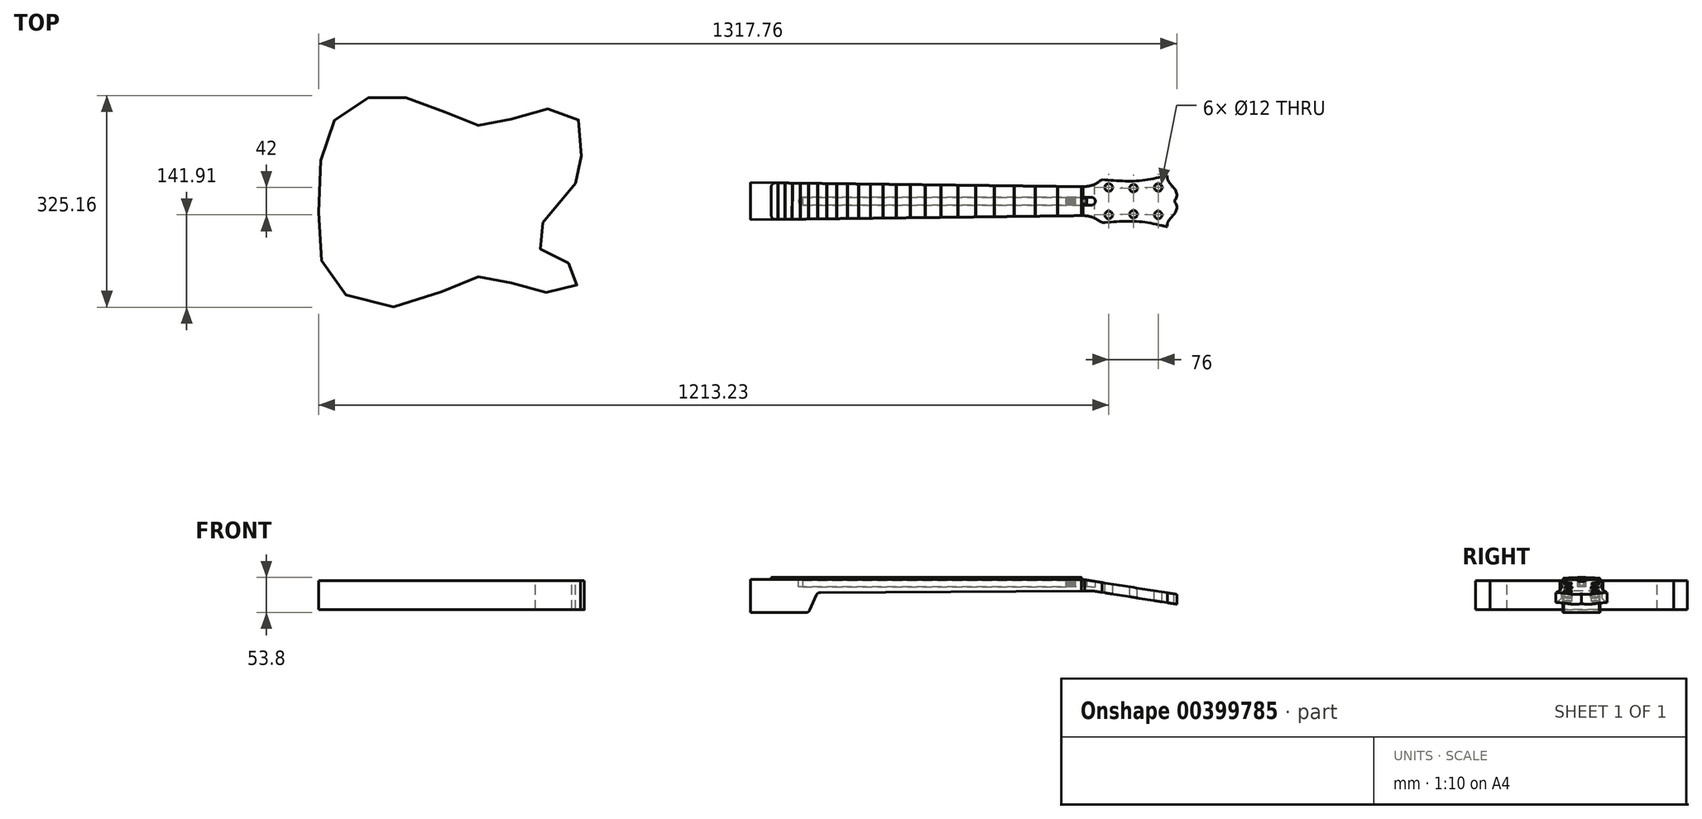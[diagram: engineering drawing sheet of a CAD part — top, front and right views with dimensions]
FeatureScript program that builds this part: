
annotation { "Feature Type Name" : "Feature", "Feature Type Description" : "" }
export const myFeature = defineFeature(function(context is Context, id is Id, definition is map)
    precondition{}
    {
        {
            var Q0;
            Q0=qCreatedBy(makeId("Top.planeOp"),FACE);
            var sketch = newSketch(context, id + "F0", { "sketchPlane" : qUnion([Q0])});
            skLineSegment(sketch, "E0", {"start": v(-323.85, 0) * mm, "end": v(323.85, 0) * mm, "construction": true});
            skLineSegment(sketch, "E1", {"start": v(323.85, 22.23) * mm, "end": v(323.85, -22.22) * mm, "construction": true});
            skLineSegment(sketch, "E2", {"start": v(-323.85, 26.25) * mm, "end": v(-323.85, -26.25) * mm, "construction": true});
            skLineSegment(sketch, "E3", {"start": v(-323.85, 26.25) * mm, "end": v(-323.85, 30.25) * mm, "construction": true});
            skLineSegment(sketch, "E4.MirrorCS", {"start": v(-323.85, -26.25) * mm, "end": v(-323.85, -30.25) * mm, "construction": true});
            skLineSegment(sketch, "E5", {"start": v(-323.85, 30.25) * mm, "end": v(323.85, 22.23) * mm, "construction": true});
            skLineSegment(sketch, "E6", {"start": v(-323.85, -30.25) * mm, "end": v(323.85, -22.23) * mm, "construction": true});
            skPoint(sketch, "E7", {"position": v(287.5, 0) * mm});
            skPoint(sketch, "E8", {"position": v(253.19, 0) * mm});
            skPoint(sketch, "E9", {"position": v(220.8, 0) * mm});
            skPoint(sketch, "E10", {"position": v(190.22, 0) * mm});
            skPoint(sketch, "E11", {"position": v(161.37, 0) * mm});
            skPoint(sketch, "E12", {"position": v(134.14, 0) * mm});
            skPoint(sketch, "E13", {"position": v(108.43, 0) * mm});
            skPoint(sketch, "E14", {"position": v(84.18, 0) * mm});
            skPoint(sketch, "E15", {"position": v(61.26, 0) * mm});
            skPoint(sketch, "E16", {"position": v(39.65, 0) * mm});
            skPoint(sketch, "E17", {"position": v(19.25, 0) * mm});
            skPoint(sketch, "E18", {"position": v(0, 0) * mm});
            skPoint(sketch, "E19", {"position": v(-18.19, 0) * mm});
            skPoint(sketch, "E20", {"position": v(-35.33, 0) * mm});
            skPoint(sketch, "E21", {"position": v(-51.54, 0) * mm});
            skPoint(sketch, "E22", {"position": v(-66.83, 0) * mm});
            skPoint(sketch, "E23", {"position": v(-81.25, 0) * mm});
            skPoint(sketch, "E24", {"position": v(-94.87, 0) * mm});
            skPoint(sketch, "E25", {"position": v(-107.72, 0) * mm});
            skPoint(sketch, "E26", {"position": v(-119.86, 0) * mm});
            skPoint(sketch, "E27", {"position": v(-131.32, 0) * mm});
            skPoint(sketch, "E28", {"position": v(-142.11, 0) * mm});
            skPoint(sketch, "E29", {"position": v(-152.32, 0) * mm});
            skLineSegment(sketch, "E30", {"start": v(-152.32, 0) * mm, "end": v(-152.32, -28.13) * mm, "construction": true});
            skLineSegment(sketch, "E31", {"start": v(-152.32, -28.13) * mm, "end": v(-152.32, 28.13) * mm, "construction": true});
            skLineSegment(sketch, "E32", {"start": v(-142.11, 0) * mm, "end": v(-142.11, -28) * mm, "construction": true});
            skLineSegment(sketch, "E33", {"start": v(-142.11, -28) * mm, "end": v(-142.11, 28) * mm, "construction": true});
            skLineSegment(sketch, "E34", {"start": v(-142.11, 28) * mm, "end": v(-131.32, 27.87) * mm, "construction": true});
            skLineSegment(sketch, "E35", {"start": v(-131.32, 0) * mm, "end": v(-131.32, -27.87) * mm, "construction": true});
            skLineSegment(sketch, "E36", {"start": v(-131.32, -27.87) * mm, "end": v(-131.32, 27.87) * mm, "construction": true});
            skLineSegment(sketch, "E37", {"start": v(-119.86, 0) * mm, "end": v(-120.2, -27.73) * mm, "construction": true});
            skLineSegment(sketch, "E38", {"start": v(-107.72, 0) * mm, "end": v(-107.72, 27.57) * mm, "construction": true});
            skLineSegment(sketch, "E39", {"start": v(-107.72, 27.57) * mm, "end": v(-107.72, -27.57) * mm, "construction": true});
            skLineSegment(sketch, "E40", {"start": v(-94.87, 0) * mm, "end": v(-94.87, 27.41) * mm, "construction": true});
            skLineSegment(sketch, "E41", {"start": v(-94.87, 27.41) * mm, "end": v(-94.87, -27.41) * mm, "construction": true});
            skLineSegment(sketch, "E42", {"start": v(-81.25, 0) * mm, "end": v(-81.25, 27.24) * mm, "construction": true});
            skLineSegment(sketch, "E43", {"start": v(-81.25, 27.24) * mm, "end": v(-81.25, -27.24) * mm, "construction": true});
            skLineSegment(sketch, "E44", {"start": v(-66.83, 0) * mm, "end": v(-66.83, 27.07) * mm, "construction": true});
            skLineSegment(sketch, "E45", {"start": v(-66.83, 27.07) * mm, "end": v(-66.83, -27.07) * mm, "construction": true});
            skLineSegment(sketch, "E46", {"start": v(-51.54, 0) * mm, "end": v(-51.54, 26.88) * mm, "construction": true});
            skLineSegment(sketch, "E47", {"start": v(-51.54, 26.88) * mm, "end": v(-51.54, -26.88) * mm, "construction": true});
            skLineSegment(sketch, "E48", {"start": v(-35.33, 0) * mm, "end": v(-35.33, 26.68) * mm, "construction": true});
            skLineSegment(sketch, "E49", {"start": v(-35.33, 26.68) * mm, "end": v(-35.33, -26.68) * mm, "construction": true});
            skLineSegment(sketch, "E50", {"start": v(-18.19, 0) * mm, "end": v(-18.19, 26.46) * mm, "construction": true});
            skLineSegment(sketch, "E51", {"start": v(-18.19, 26.46) * mm, "end": v(-18.19, -26.46) * mm, "construction": true});
            skLineSegment(sketch, "E52", {"start": v(19.25, 0) * mm, "end": v(19.25, 26) * mm, "construction": true});
            skLineSegment(sketch, "E53", {"start": v(19.25, 26) * mm, "end": v(19.25, -26) * mm, "construction": true});
            skLineSegment(sketch, "E54", {"start": v(39.65, 0) * mm, "end": v(39.65, 25.75) * mm, "construction": true});
            skLineSegment(sketch, "E55", {"start": v(39.65, 25.75) * mm, "end": v(39.65, -25.75) * mm, "construction": true});
            skLineSegment(sketch, "E56", {"start": v(61.26, 0) * mm, "end": v(61.26, 25.48) * mm, "construction": true});
            skLineSegment(sketch, "E57", {"start": v(61.26, 25.48) * mm, "end": v(61.26, -25.48) * mm, "construction": true});
            skLineSegment(sketch, "E58", {"start": v(84.18, 0) * mm, "end": v(84.18, 25.2) * mm, "construction": true});
            skLineSegment(sketch, "E59", {"start": v(84.18, 25.2) * mm, "end": v(84.18, -25.2) * mm, "construction": true});
            skLineSegment(sketch, "E60", {"start": v(108.43, 0) * mm, "end": v(108.43, 24.9) * mm, "construction": true});
            skLineSegment(sketch, "E61", {"start": v(108.43, 24.9) * mm, "end": v(108.43, -24.9) * mm, "construction": true});
            skLineSegment(sketch, "E62", {"start": v(134.14, 0) * mm, "end": v(134.14, 24.58) * mm, "construction": true});
            skLineSegment(sketch, "E63", {"start": v(134.14, 24.58) * mm, "end": v(134.14, -24.58) * mm, "construction": true});
            skLineSegment(sketch, "E64", {"start": v(161.37, 0) * mm, "end": v(161.37, 24.24) * mm, "construction": true});
            skLineSegment(sketch, "E65", {"start": v(161.37, 24.24) * mm, "end": v(161.37, -24.24) * mm, "construction": true});
            skLineSegment(sketch, "E66", {"start": v(190.22, 0) * mm, "end": v(190.22, 23.88) * mm, "construction": true});
            skLineSegment(sketch, "E67", {"start": v(190.22, 23.88) * mm, "end": v(190.22, -23.88) * mm, "construction": true});
            skLineSegment(sketch, "E68", {"start": v(220.8, 0) * mm, "end": v(220.8, 23.5) * mm});
            skLineSegment(sketch, "E69", {"start": v(220.8, 23.5) * mm, "end": v(220.8, -23.5) * mm, "construction": true});
            skLineSegment(sketch, "E70", {"start": v(253.19, 0) * mm, "end": v(253.19, 23.1) * mm, "construction": true});
            skLineSegment(sketch, "E71", {"start": v(253.19, 23.1) * mm, "end": v(253.19, -23.1) * mm, "construction": true});
            skLineSegment(sketch, "E72", {"start": v(287.5, 0) * mm, "end": v(287.5, 22.68) * mm, "construction": true});
            skLineSegment(sketch, "E73", {"start": v(287.5, 22.68) * mm, "end": v(287.5, -22.68) * mm, "construction": true});
            skLineSegment(sketch, "E74", {"start": v(0, 0) * mm, "end": v(0, 26.24) * mm, "construction": true});
            skLineSegment(sketch, "E75", {"start": v(0, 26.24) * mm, "end": v(0, -26.24) * mm, "construction": true});
            skLineSegment(sketch, "E76", {"start": v(-119.86, 0) * mm, "end": v(-119.86, 27.72) * mm, "construction": true});
            skLineSegment(sketch, "E77", {"start": v(323.85, 0) * mm, "end": v(-317.5, 0) * mm, "construction": true});
            skLineSegment(sketch, "E78", {"start": v(-317.08, 33.5) * mm, "end": v(-317.92, -33.5) * mm, "construction": true});
            skPoint(sketch, "E79", {"position": v(-317.08, 33.5) * mm});
            skPoint(sketch, "E80", {"position": v(-317.92, -33.5) * mm});
            skLineSegment(sketch, "E81", {"start": v(-317.08, 33.5) * mm, "end": v(-347.56, 33.88) * mm, "construction": true});
            skPoint(sketch, "E82", {"position": v(-347.56, 33.88) * mm});
            skLineSegment(sketch, "E83.MirrorCS", {"start": v(-317.08, -33.5) * mm, "end": v(-347.56, -33.88) * mm, "construction": true});
            skPoint(sketch, "E84.MirrorP", {"position": v(-347.56, -33.88) * mm});
            skLineSegment(sketch, "E85", {"start": v(-347.56, -33.88) * mm, "end": v(-347.56, 33.88) * mm, "construction": true});
            skPoint(sketch, "E86", {"position": v(-347.56, 0) * mm});
            skLineSegment(sketch, "E87", {"start": v(323.85, 0) * mm, "end": v(328.61, 0) * mm, "construction": true});
            skLineSegment(sketch, "E88", {"start": v(328.61, -22.22) * mm, "end": v(328.61, 22.23) * mm, "construction": true});
            skSolve(sketch);
        }
        {
            var Q0;
            Q0=qCreatedBy(makeId("Top.planeOp"),FACE);
            var sketch = newSketch(context, id + "F1", { "sketchPlane" : qUnion([Q0])});
            skLineSegment(sketch, "E89", {"start": v(-184.07, 44.45) * mm, "end": v(-184.07, -44.45) * mm, "construction": true});
            skPoint(sketch, "E90.0", {"position": v(-152.32, 0) * mm});
            skLineSegment(sketch, "E91", {"start": v(-152.32, 0) * mm, "end": v(-184.07, 0) * mm, "construction": true});
            skLineSegment(sketch, "E92.bottom", {"start": v(-184.07, 44.45) * mm, "end": v(476.33, 44.45) * mm});
            skLineSegment(sketch, "E92.top", {"start": v(-184.07, -44.45) * mm, "end": v(476.33, -44.45) * mm});
            skLineSegment(sketch, "E92.left", {"start": v(-184.07, 44.45) * mm, "end": v(-184.07, -44.45) * mm});
            skLineSegment(sketch, "E92.right", {"start": v(476.33, 44.45) * mm, "end": v(476.33, -44.45) * mm});
            skSolve(sketch);
        }
        {
            var Q0;
            Q0 = qSketchRegion(id + "F1", true);
            extrude(context, id + "F2", {"entities" : qUnion([Q0]), "oppositeDirection" : true, "depth" : 63.5 * mm});
        }
        {
            var Q0;
            Q0=makeQuery(id+"F2.opExtrude","CAP_FACE",FACE,{"disambiguationData":[OSD([sQuery(id+"F1.wireOp",EDGE,"E92.bottom"),sQuery(id+"F1.wireOp",EDGE,"E92.top"),sQuery(id+"F1.wireOp",EDGE,"E92.left"),sQuery(id+"F1.wireOp",EDGE,"E92.right")])],"isStart":true});
            cPlane(context, id + "F3", {"entities" : qUnion([Q0]), "cplaneType" : CPlaneType.OFFSET, "offset" : 2 * mm, "oppositeDirection" : true, "width" : 152.4 * mm, "height" : 152.4 * mm});
        }
        {
            var Q0;
            Q0=makeQuery(id+"F2.opExtrude","CAP_FACE",FACE,{"disambiguationData":[OSD([sQuery(id+"F1.wireOp",EDGE,"E92.bottom"),sQuery(id+"F1.wireOp",EDGE,"E92.top"),sQuery(id+"F1.wireOp",EDGE,"E92.left"),sQuery(id+"F1.wireOp",EDGE,"E92.right")])],"isStart":true});
            var sketch = newSketch(context, id + "F4", { "sketchPlane" : qUnion([Q0])});
            skPoint(sketch, "E93.0", {"position": v(326.23, 0) * mm});
            skLineSegment(sketch, "E94", {"start": v(326.23, 0) * mm, "end": v(345.28, 0) * mm, "construction": true});
            skLineSegment(sketch, "E95", {"start": v(326.23, 0) * mm, "end": v(-110.33, 0) * mm, "construction": true});
            skLineSegment(sketch, "E96", {"start": v(345.28, 0) * mm, "end": v(345.28, -6) * mm, "construction": true});
            skLineSegment(sketch, "E97.bottom", {"start": v(339.28, 6) * mm, "end": v(-104.33, 6) * mm});
            skLineSegment(sketch, "E97.top", {"start": v(339.28, -6) * mm, "end": v(-104.33, -6) * mm});
            skLineSegment(sketch, "E97.left", {"start": v(345.28, 6) * mm, "end": v(345.28, 0) * mm});
            skLineSegment(sketch, "E97.right", {"start": v(-110.33, 0) * mm, "end": v(-110.33, 0) * mm});
            skPoint(sketch, "E98.visualSharp", {"position": v(-110.33, 6) * mm});
            skArc(sketch, "E98.filletArc", {"start": v(-104.33, 6) * mm, "mid": v(-108.57, 4.24) * mm, "end": v(-110.33, 0) * mm});
            skPoint(sketch, "E99.visualSharp", {"position": v(-110.33, -6) * mm});
            skArc(sketch, "E99.filletArc", {"start": v(-110.33, 0) * mm, "mid": v(-108.57, -4.24) * mm, "end": v(-104.33, -6) * mm});
            skPoint(sketch, "E100.visualSharp", {"position": v(345.28, -6) * mm});
            skArc(sketch, "E100.filletArc", {"start": v(339.28, -6) * mm, "mid": v(343.52, -4.24) * mm, "end": v(345.28, 0) * mm});
            skPoint(sketch, "E101.visualSharp", {"position": v(345.28, 6) * mm});
            skArc(sketch, "E101.filletArc", {"start": v(345.28, 0) * mm, "mid": v(343.52, 4.24) * mm, "end": v(339.28, 6) * mm});
            skSolve(sketch);
        }
        {
            var Q0;
            Q0 = qSketchRegion(id + "F4", true);
            extrude(context, id + "F5", {"entities" : qUnion([Q0]), "operationType" : NewBodyOperationType.REMOVE, "oppositeDirection" : true, "depth" : 11.5 * mm});
        }
        {
            var Q0;
            Q0=makeQuery(id+"F2.opExtrude","SWEPT_FACE",FACE,{"disambiguationData":[OSD([sQuery(id+"F1.wireOp",EDGE,"E92.top")])]});
            var sketch = newSketch(context, id + "F6", { "sketchPlane" : qUnion([Q0])});
            skPoint(sketch, "E102.0", {"position": v(328.61, 0) * mm});
            skPoint(sketch, "E103.0", {"position": v(326.23, 0) * mm});
            skLineSegment(sketch, "E104", {"start": v(326.23, 0) * mm, "end": v(326.23, -63.5) * mm, "construction": true});
            skLineSegment(sketch, "E105", {"start": v(328.61, 0) * mm, "end": v(328.61, -63.5) * mm, "construction": true});
            skLineSegment(sketch, "E106", {"start": v(326.23, 0) * mm, "end": v(476.33, -23.77) * mm});
            skLineSegment(sketch, "E107", {"start": v(326.23, 0) * mm, "end": v(476.33, 0) * mm});
            skLineSegment(sketch, "E108", {"start": v(476.33, 0) * mm, "end": v(476.33, -23.77) * mm});
            skSolve(sketch);
        }
        {
            var Q0;
            Q0=makeQuery(id+"F6.imprint","IMPRINT",FACE,{"disambiguationData":[TD([[makeQuery(id+"F6.imprint","IMPRINT",EDGE,{"derivedFrom":sQuery(id+"F6.wireOp",EDGE,"E106")}),1.0]])]});
            var Q1;
            Q1=makeQuery(id+"F2.opExtrude","SWEPT_BODY",BODY,{"disambiguationData":[OSD([sQuery(id+"F1.wireOp",EDGE,"E92.bottom"),sQuery(id+"F1.wireOp",EDGE,"E92.top"),sQuery(id+"F1.wireOp",EDGE,"E92.left"),sQuery(id+"F1.wireOp",EDGE,"E92.right")])]});
            extrude(context, id + "F7", {"entities" : qUnion([Q0]), "operationType" : NewBodyOperationType.REMOVE, "endBound" : BoundingType.UP_TO_BODY, "oppositeDirection" : true, "endBoundEntityBody" : qUnion([Q1]), "depth" : 25.4 * mm});
        }
        {
            var Q0;
            Q0=makeQuery(id+"F2.opExtrude","SWEPT_FACE",FACE,{"disambiguationData":[OSD([sQuery(id+"F1.wireOp",EDGE,"E92.top")])]});
            var sketch = newSketch(context, id + "F8", { "sketchPlane" : qUnion([Q0])});
            skLineSegment(sketch, "E109", {"start": v(401.28, -11.89) * mm, "end": v(398.93, -26.7) * mm, "construction": true});
            skPoint(sketch, "E110.0", {"position": v(328.61, 0) * mm});
            skLineSegment(sketch, "E111.0", {"start": v(326.23, 0) * mm, "end": v(476.33, -23.77) * mm, "construction": true});
            skLineSegment(sketch, "E112", {"start": v(476.33, -23.77) * mm, "end": v(326.23, 0) * mm});
            skPoint(sketch, "E113.0", {"position": v(-119.86, 0) * mm});
            skLineSegment(sketch, "E114", {"start": v(-119.86, 0) * mm, "end": v(-119.86, -63.5) * mm, "construction": true});
            skLineSegment(sketch, "E115", {"start": v(326.23, 0) * mm, "end": v(326.23, -18) * mm, "construction": true});
            skPoint(sketch, "E116.0", {"position": v(-81.25, 0) * mm});
            skPoint(sketch, "E117.0", {"position": v(-94.87, 0) * mm});
            skLineSegment(sketch, "E118", {"start": v(-94.87, 0) * mm, "end": v(-94.87, -63.5) * mm, "construction": true});
            skLineSegment(sketch, "E119", {"start": v(-81.25, 0) * mm, "end": v(-81.25, -20) * mm, "construction": true});
            skLineSegment(sketch, "E120", {"start": v(-77.14, -19.98) * mm, "end": v(343.46, -17.92) * mm});
            skLineSegment(sketch, "E121", {"start": v(-82.92, -23.76) * mm, "end": v(-93.2, -47.02) * mm});
            skLineSegment(sketch, "E122", {"start": v(-99, -50.8) * mm, "end": v(-184.07, -50.8) * mm});
            skLineSegment(sketch, "E123", {"start": v(-184.07, -50.8) * mm, "end": v(-184.07, 0) * mm});
            skLineSegment(sketch, "E124", {"start": v(-184.07, 0) * mm, "end": v(328.61, 0) * mm});
            skPoint(sketch, "E125.visualSharp", {"position": v(-81.25, -20) * mm});
            skArc(sketch, "E125.filletArc", {"start": v(-77.14, -19.98) * mm, "mid": v(-80.59, -21.02) * mm, "end": v(-82.92, -23.76) * mm});
            skPoint(sketch, "E126.visualSharp", {"position": v(-94.87, -50.8) * mm});
            skArc(sketch, "E126.filletArc", {"start": v(-99, -50.8) * mm, "mid": v(-95.54, -49.77) * mm, "end": v(-93.2, -47.02) * mm});
            skLineSegment(sketch, "E127", {"start": v(473.98, -38.59) * mm, "end": v(343.46, -17.92) * mm});
            skLineSegment(sketch, "E128", {"start": v(476.33, -23.77) * mm, "end": v(470.03, -63.5) * mm});
            skSolve(sketch);
        }
        {
            var Q0;
            Q0 = qSketchRegion(id + "F8", true);
            var Q1;
            Q1=makeQuery(id+"F2.opExtrude","SWEPT_BODY",BODY,{"disambiguationData":[OSD([sQuery(id+"F1.wireOp",EDGE,"E92.bottom"),sQuery(id+"F1.wireOp",EDGE,"E92.top"),sQuery(id+"F1.wireOp",EDGE,"E92.left"),sQuery(id+"F1.wireOp",EDGE,"E92.right")])]});
            extrude(context, id + "F9", {"entities" : qUnion([Q0]), "operationType" : NewBodyOperationType.INTERSECT, "endBound" : BoundingType.UP_TO_BODY, "oppositeDirection" : true, "endBoundEntityBody" : qUnion([Q1]), "depth" : 101.6 * mm});
        }
        {
            var Q0;
            Q0=makeQuery(id+"F2.opExtrude","CAP_FACE",FACE,{"disambiguationData":[OSD([sQuery(id+"F1.wireOp",EDGE,"E92.bottom"),sQuery(id+"F1.wireOp",EDGE,"E92.top"),sQuery(id+"F1.wireOp",EDGE,"E92.left"),sQuery(id+"F1.wireOp",EDGE,"E92.right")])],"isStart":true});
            var sketch = newSketch(context, id + "F10", { "sketchPlane" : qUnion([Q0])});
            skLineSegment(sketch, "E129.0", {"start": v(323.85, 0) * mm, "end": v(-317.5, 0) * mm, "construction": true});
            skLineSegment(sketch, "E130", {"start": v(323.85, 0) * mm, "end": v(472.48, 0) * mm, "construction": true});
            skLineSegment(sketch, "E131.0", {"start": v(328.61, -22.22) * mm, "end": v(328.61, 22.23) * mm, "construction": true});
            skLineSegment(sketch, "E132.0", {"start": v(323.85, 22.23) * mm, "end": v(323.85, -22.22) * mm, "construction": true});
            skLineSegment(sketch, "E133", {"start": v(365.85, 0) * mm, "end": v(365.85, 21) * mm, "construction": true});
            skLineSegment(sketch, "E134", {"start": v(403.85, 0) * mm, "end": v(403.85, 20) * mm, "construction": true});
            skLineSegment(sketch, "E135", {"start": v(441.85, 0) * mm, "end": v(441.85, 21) * mm, "construction": true});
            skCircle(sketch, "E136", {"center": v(365.85, 21) * mm, "radius": 6 * mm});
            skCircle(sketch, "E137", {"center": v(403.85, 20) * mm, "radius": 6 * mm});
            skCircle(sketch, "E138", {"center": v(441.85, 21) * mm, "radius": 6 * mm});
            skCircle(sketch, "E139.MirrorC", {"center": v(365.85, -21) * mm, "radius": 6 * mm});
            skCircle(sketch, "E140.MirrorC", {"center": v(403.85, -20) * mm, "radius": 6 * mm});
            skCircle(sketch, "E141.MirrorC", {"center": v(441.85, -21) * mm, "radius": 6 * mm});
            skLineSegment(sketch, "E142", {"start": v(365.85, -21) * mm, "end": v(355.85, -21) * mm, "construction": true});
            skLineSegment(sketch, "E143", {"start": v(355.85, -21) * mm, "end": v(355.85, -33) * mm, "construction": true});
            skLineSegment(sketch, "E144", {"start": v(355.85, -33) * mm, "end": v(470.76, -33) * mm, "construction": true});
            skPoint(sketch, "E145", {"position": v(465.77, 0) * mm});
            skPoint(sketch, "E146", {"position": v(455.61, -39.35) * mm});
            skFitSpline(sketch, "E147", {"points": [v(465.77, 0) * mm, v(469.92, -13.07) * mm, v(458.58, -28.8) * mm, v(455.61, -39.35) * mm], "startDerivative": vector(34.11, -22.35) * mm, "endDerivative": vector(7.21, -32.63) * mm});
            skFitSpline(sketch, "E148", {"points": [v(455.61, -39.35) * mm, v(411.53, -31.35) * mm, v(355.85, -33) * mm], "startDerivative": vector(-90.96, 21.97) * mm, "endDerivative": vector(-108.28, -8.76) * mm});
            skFitSpline(sketch, "E149", {"points": [v(328.61, -22.22) * mm, v(342.64, -25.24) * mm, v(355.85, -33) * mm], "startDerivative": vector(28.5, -4.66) * mm, "endDerivative": vector(25.97, -12.88) * mm});
            skFitSpline(sketch, "E150.MirrorCS", {"points": [v(328.61, 22.22) * mm, v(342.64, 25.24) * mm, v(355.85, 33) * mm], "startDerivative": vector(28.5, 4.66) * mm, "endDerivative": vector(25.97, 12.88) * mm});
            skFitSpline(sketch, "E151.MirrorCS", {"points": [v(455.61, 39.35) * mm, v(411.53, 31.35) * mm, v(355.85, 33) * mm], "startDerivative": vector(-90.96, -21.97) * mm, "endDerivative": vector(-108.28, 8.76) * mm});
            skFitSpline(sketch, "E152.MirrorCS", {"points": [v(465.77, 0) * mm, v(469.92, 13.07) * mm, v(458.58, 28.8) * mm, v(455.61, 39.35) * mm], "startDerivative": vector(34.11, 22.35) * mm, "endDerivative": vector(7.21, 32.63) * mm});
            skLineSegment(sketch, "E153", {"start": v(328.61, 22.23) * mm, "end": v(323.85, 22.23) * mm});
            skPoint(sketch, "E154.0", {"position": v(-152.32, 28.13) * mm});
            skPoint(sketch, "E155.0", {"position": v(-152.32, -28.13) * mm});
            skLineSegment(sketch, "E156", {"start": v(323.85, 22.23) * mm, "end": v(-184.07, 28.52) * mm});
            skLineSegment(sketch, "E157", {"start": v(-184.07, -28.52) * mm, "end": v(323.85, -22.22) * mm});
            skLineSegment(sketch, "E158", {"start": v(323.85, -22.22) * mm, "end": v(328.61, -22.22) * mm});
            skLineSegment(sketch, "E159", {"start": v(-184.07, 28.52) * mm, "end": v(-184.07, -28.52) * mm});
            skSolve(sketch);
        }
        {
            var Q0;
            Q0=makeQuery(id+"F10.imprint","IMPRINT",FACE,{"disambiguationData":[TD([[makeQuery(id+"F10.imprint","IMPRINT",EDGE,{"derivedFrom":sQuery(id+"F10.wireOp",EDGE,"E136")}),-1.0]])]});
            var Q1;
            {var subQ12=sQuery(id+"F10.wireOp",EDGE,"E156");Q1=makeQuery(id+"F10.imprint","IMPRINT",FACE,{"disambiguationData":[TD([[makeQuery(id+"F10.imprint","IMPRINT",EDGE,{"derivedFrom":subQ12}),1.0]])]});}
            var Q2;
            Q2=makeQuery(id+"F2.opExtrude","SWEPT_BODY",BODY,{"disambiguationData":[OSD([sQuery(id+"F1.wireOp",EDGE,"E92.bottom"),sQuery(id+"F1.wireOp",EDGE,"E92.top"),sQuery(id+"F1.wireOp",EDGE,"E92.left"),sQuery(id+"F1.wireOp",EDGE,"E92.right")])]});
            extrude(context, id + "F11", {"entities" : qUnion([Q0, Q1]), "operationType" : NewBodyOperationType.INTERSECT, "endBound" : BoundingType.UP_TO_BODY, "oppositeDirection" : true, "endBoundEntityBody" : qUnion([Q2]), "depth" : 25.4 * mm});
        }
        {
            var Q0;
            Q0=qCreatedBy(makeId("Top.planeOp"),FACE);
            cPlane(context, id + "F12", {"entities" : qUnion([Q0]), "cplaneType" : CPlaneType.OFFSET, "offset" : 11.5 * mm, "oppositeDirection" : true, "width" : 152.4 * mm, "height" : 152.4 * mm});
        }
        {
            var Q0;
            Q0=qCreatedBy(id+"F12.planeOp",FACE);
            var sketch = newSketch(context, id + "F13", { "sketchPlane" : qUnion([Q0])});
            skPoint(sketch, "E160.0", {"position": v(-104.33, 6) * mm});
            skPoint(sketch, "E161.0", {"position": v(-104.33, -6) * mm});
            skLineSegment(sketch, "E162.bottom", {"start": v(-104.33, 6) * mm, "end": v(332.23, 6) * mm});
            skLineSegment(sketch, "E162.top", {"start": v(-104.33, -6) * mm, "end": v(332.23, -6) * mm});
            skLineSegment(sketch, "E162.left", {"start": v(-104.33, 6) * mm, "end": v(-104.33, -6) * mm});
            skLineSegment(sketch, "E162.right", {"start": v(332.23, 6) * mm, "end": v(332.23, -6) * mm});
            skSolve(sketch);
        }
        {
            var Q0;
            Q0 = qSketchRegion(id + "F13", true);
            extrude(context, id + "F14", {"entities" : qUnion([Q0]), "depth" : 10.16 * mm});
        }
        {
            var Q0;
            Q0=makeQuery(id+"F14.opExtrude","SWEPT_FACE",FACE,{"disambiguationData":[OSD([sQuery(id+"F13.wireOp",EDGE,"E162.bottom")])]});
            cPlane(context, id + "F15", {"entities" : qUnion([Q0]), "cplaneType" : CPlaneType.OFFSET, "offset" : 6 * mm, "oppositeDirection" : true, "width" : 152.4 * mm, "height" : 152.4 * mm});
        }
        {
            var Q0;
            Q0=makeQuery(id+"F14.opExtrude","SWEPT_FACE",FACE,{"disambiguationData":[OSD([sQuery(id+"F13.wireOp",EDGE,"E162.right")])]});
            var sketch = newSketch(context, id + "F16", { "sketchPlane" : qUnion([Q0])});
            skLineSegment(sketch, "E163", {"start": v(-6, -6.42) * mm, "end": v(6, -6.42) * mm, "construction": true});
            skLineSegment(sketch, "E164", {"start": v(0, -11.5) * mm, "end": v(0, -1.34) * mm, "construction": true});
            skPoint(sketch, "E165", {"position": v(0, -6.42) * mm});
            skCircle(sketch, "E166", {"center": v(0, -6.42) * mm, "radius": 7.86 * mm});
            skCircle(sketch, "E167", {"center": v(0, -6.42) * mm, "radius": 4.5 * mm});
            skCircle(sketch, "E168", {"center": v(0, -6.42) * mm, "radius": 2.5 * mm});
            skCircle(sketch, "E169.cCircle", {"center": v(0, -6.42) * mm, "radius": 2.5 * mm, "construction": true});
            skLineSegment(sketch, "E169.0", {"start": v(0.73, -3.63) * mm, "end": v(2.78, -5.65) * mm});
            skLineSegment(sketch, "E169.1", {"start": v(2.78, -5.65) * mm, "end": v(2.06, -8.45) * mm});
            skLineSegment(sketch, "E169.2", {"start": v(2.06, -8.45) * mm, "end": v(-0.73, -9.21) * mm});
            skLineSegment(sketch, "E169.3", {"start": v(-0.73, -9.21) * mm, "end": v(-2.78, -7.19) * mm});
            skLineSegment(sketch, "E169.4", {"start": v(-2.78, -7.19) * mm, "end": v(-2.06, -4.4) * mm});
            skLineSegment(sketch, "E169.5", {"start": v(-2.06, -4.4) * mm, "end": v(0.73, -3.63) * mm});
            skPoint(sketch, "E169.0.midPoint", {"position": v(1.76, -4.64) * mm});
            skSolve(sketch);
        }
        {
            var Q0;
            Q0=makeQuery(id+"F16.imprint","IMPRINT",FACE,{"disambiguationData":[TD([[makeQuery(id+"F16.imprint","IMPRINT",EDGE,{"derivedFrom":sQuery(id+"F16.wireOp",EDGE,"E167")}),-1.0]])]});
            var Q1;
            {var subQ0=sQuery(id+"F16.wireOp",EDGE,"E169.5");var subQ1=sQuery(id+"F16.wireOp",EDGE,"E168");var subQ2=makeQuery(id+"F16.imprint","INTERSECT",VERTEX,{"derivedFrom":[subQ1,subQ0]});Q1=makeQuery(id+"F16.imprint","IMPRINT",FACE,{"disambiguationData":[TD([[makeQuery(id+"F16.imprint","IMPRINT",EDGE,{"disambiguationData":[TD([[subQ2,-1.0]])],"derivedFrom":subQ1}),-1.0]])]});}
            var Q2;
            {var subQ0=sQuery(id+"F16.wireOp",EDGE,"E169.5");var subQ1=sQuery(id+"F16.wireOp",EDGE,"E168");var subQ2=makeQuery(id+"F16.imprint","INTERSECT",VERTEX,{"derivedFrom":[subQ1,subQ0]});Q2=makeQuery(id+"F16.imprint","IMPRINT",FACE,{"disambiguationData":[TD([[makeQuery(id+"F16.imprint","IMPRINT",EDGE,{"disambiguationData":[TD([[subQ2,1.0]])],"derivedFrom":subQ1}),-1.0]])]});}
            var Q3;
            {var subQ0=sQuery(id+"F16.wireOp",EDGE,"E169.0");var subQ1=sQuery(id+"F16.wireOp",EDGE,"E168");var subQ2=makeQuery(id+"F16.imprint","INTERSECT",VERTEX,{"derivedFrom":[subQ1,subQ0]});Q3=makeQuery(id+"F16.imprint","IMPRINT",FACE,{"disambiguationData":[TD([[makeQuery(id+"F16.imprint","IMPRINT",EDGE,{"disambiguationData":[TD([[subQ2,1.0]])],"derivedFrom":subQ1}),-1.0]])]});}
            var Q4;
            {var subQ0=sQuery(id+"F16.wireOp",EDGE,"E169.2");var subQ1=sQuery(id+"F16.wireOp",EDGE,"E168");var subQ2=makeQuery(id+"F16.imprint","INTERSECT",VERTEX,{"derivedFrom":[subQ1,subQ0]});Q4=makeQuery(id+"F16.imprint","IMPRINT",FACE,{"disambiguationData":[TD([[makeQuery(id+"F16.imprint","IMPRINT",EDGE,{"disambiguationData":[TD([[subQ2,-1.0]])],"derivedFrom":subQ1}),-1.0]])]});}
            var Q5;
            {var subQ0=sQuery(id+"F16.wireOp",EDGE,"E169.3");var subQ1=sQuery(id+"F16.wireOp",EDGE,"E168");var subQ2=makeQuery(id+"F16.imprint","INTERSECT",VERTEX,{"derivedFrom":[subQ1,subQ0]});Q5=makeQuery(id+"F16.imprint","IMPRINT",FACE,{"disambiguationData":[TD([[makeQuery(id+"F16.imprint","IMPRINT",EDGE,{"disambiguationData":[TD([[subQ2,-1.0]])],"derivedFrom":subQ1}),-1.0]])]});}
            var Q6;
            {var subQ0=sQuery(id+"F16.wireOp",EDGE,"E169.4");var subQ1=sQuery(id+"F16.wireOp",EDGE,"E168");var subQ2=makeQuery(id+"F16.imprint","INTERSECT",VERTEX,{"derivedFrom":[subQ1,subQ0]});Q6=makeQuery(id+"F16.imprint","IMPRINT",FACE,{"disambiguationData":[TD([[makeQuery(id+"F16.imprint","IMPRINT",EDGE,{"disambiguationData":[TD([[subQ2,-1.0]])],"derivedFrom":subQ1}),-1.0]])]});}
            var Q7;
            {var subQ0=sQuery(id+"F16.wireOp",EDGE,"E168");var subQ4=makeQuery(id+"F16.imprint","INTERSECT",VERTEX,{"derivedFrom":[subQ0,sQuery(id+"F16.wireOp",EDGE,"E169.5")]});Q7=makeQuery(id+"F16.imprint","IMPRINT",FACE,{"disambiguationData":[TD([[makeQuery(id+"F16.imprint","IMPRINT",EDGE,{"disambiguationData":[TD([[subQ4,1.0]])],"derivedFrom":subQ0}),1.0]])]});}
            extrude(context, id + "F17", {"entities" : qUnion([Q0, Q1, Q2, Q3, Q4, Q5, Q6, Q7]), "operationType" : NewBodyOperationType.REMOVE, "oppositeDirection" : true, "depth" : 31.75 * mm});
        }
        {
            var Q0;
            Q0=makeQuery(id+"F14.opExtrude","SWEPT_FACE",FACE,{"disambiguationData":[OSD([sQuery(id+"F13.wireOp",EDGE,"E162.top")])]});
            var sketch = newSketch(context, id + "F18", { "sketchPlane" : qUnion([Q0])});
            skLineSegment(sketch, "E170.bottom", {"start": v(-104.33, -1.34) * mm, "end": v(323.85, -1.34) * mm});
            skLineSegment(sketch, "E170.top", {"start": v(-104.33, 0) * mm, "end": v(323.85, 0) * mm});
            skLineSegment(sketch, "E170.left", {"start": v(-104.33, -1.34) * mm, "end": v(-104.33, 0) * mm});
            skLineSegment(sketch, "E170.right", {"start": v(323.85, -1.34) * mm, "end": v(323.85, 0) * mm});
            skSolve(sketch);
        }
        {
            var Q0;
            Q0 = qSketchRegion(id + "F18", true);
            extrude(context, id + "F19", {"entities" : qUnion([Q0]), "oppositeDirection" : true, "depth" : 12 * mm});
        }
        {
            var Q0;
            Q0=makeQuery(id+"F2.opExtrude","CAP_FACE",FACE,{"disambiguationData":[OSD([sQuery(id+"F1.wireOp",EDGE,"E92.bottom"),sQuery(id+"F1.wireOp",EDGE,"E92.top"),sQuery(id+"F1.wireOp",EDGE,"E92.left"),sQuery(id+"F1.wireOp",EDGE,"E92.right")])],"isStart":true});
            var sketch = newSketch(context, id + "F20", { "sketchPlane" : qUnion([Q0])});
            skPoint(sketch, "E171.0", {"position": v(-152.32, 28.13) * mm});
            skPoint(sketch, "E172.0", {"position": v(-152.32, -28.13) * mm});
            skPoint(sketch, "E173.0", {"position": v(323.85, -22.22) * mm});
            skPoint(sketch, "E174.0", {"position": v(323.85, 22.23) * mm});
            skLineSegment(sketch, "E175", {"start": v(-152.32, 21.7) * mm, "end": v(-152.32, -21.7) * mm});
            skLineSegment(sketch, "E176", {"start": v(323.85, -22.22) * mm, "end": v(323.85, 22.23) * mm});
            skLineSegment(sketch, "E177", {"start": v(-145.9, 28.05) * mm, "end": v(323.85, 22.23) * mm});
            skLineSegment(sketch, "E178", {"start": v(323.85, -22.22) * mm, "end": v(-145.9, -28.05) * mm});
            skArc(sketch, "E179.filletArc", {"start": v(-145.9, 28.05) * mm, "mid": v(-150.44, 26.21) * mm, "end": v(-152.32, 21.7) * mm});
            skArc(sketch, "E180.filletArc", {"start": v(-152.32, -21.7) * mm, "mid": v(-150.44, -26.21) * mm, "end": v(-145.9, -28.05) * mm});
            skSolve(sketch);
        }
        {
            var Q0;
            Q0 = qSketchRegion(id + "F20", true);
            extrude(context, id + "F21", {"entities" : qUnion([Q0]), "depth" : 3 * mm});
        }
        {
            var Q0;
            Q0=makeQuery(id+"F21.opExtrude","CAP_FACE",FACE,{"disambiguationData":[OSD([sQuery(id+"F20.wireOp",EDGE,"E175"),sQuery(id+"F20.wireOp",EDGE,"E176"),sQuery(id+"F20.wireOp",EDGE,"E177"),sQuery(id+"F20.wireOp",EDGE,"E178")])],"isStart":false});
            var sketch = newSketch(context, id + "F22", { "sketchPlane" : qUnion([Q0])});
            skLineSegment(sketch, "E181.bottom", {"start": v(287.21, 22.68) * mm, "end": v(287.8, 22.68) * mm});
            skLineSegment(sketch, "E181.top", {"start": v(287.21, -22.68) * mm, "end": v(287.8, -22.68) * mm});
            skLineSegment(sketch, "E181.left", {"start": v(287.21, 22.68) * mm, "end": v(287.21, -22.68) * mm});
            skLineSegment(sketch, "E181.right", {"start": v(287.8, 22.68) * mm, "end": v(287.8, -22.68) * mm});
            skPoint(sketch, "E182.0", {"position": v(287.5, -22.68) * mm});
            skPoint(sketch, "E183.0", {"position": v(253.19, 23.1) * mm});
            skPoint(sketch, "E184.0", {"position": v(220.8, 23.5) * mm});
            skPoint(sketch, "E185.0", {"position": v(190.22, 23.88) * mm});
            skPoint(sketch, "E186.0", {"position": v(161.37, 24.24) * mm});
            skPoint(sketch, "E187.0", {"position": v(134.14, 24.58) * mm});
            skPoint(sketch, "E188.0", {"position": v(108.43, 24.9) * mm});
            skPoint(sketch, "E189.0", {"position": v(253.19, -23.1) * mm});
            skPoint(sketch, "E190.0", {"position": v(220.8, -23.5) * mm});
            skPoint(sketch, "E191.0", {"position": v(190.22, -23.88) * mm});
            skPoint(sketch, "E192.0", {"position": v(161.37, -24.24) * mm});
            skPoint(sketch, "E193.0", {"position": v(134.14, -24.58) * mm});
            skPoint(sketch, "E194.0", {"position": v(108.43, -24.9) * mm});
            skLineSegment(sketch, "E195.bottom", {"start": v(252.9, 23.1) * mm, "end": v(253.48, 23.1) * mm});
            skLineSegment(sketch, "E195.top", {"start": v(252.9, -23.1) * mm, "end": v(253.48, -23.1) * mm});
            skLineSegment(sketch, "E195.left", {"start": v(252.9, 23.1) * mm, "end": v(252.9, -23.1) * mm});
            skLineSegment(sketch, "E195.right", {"start": v(253.48, 23.1) * mm, "end": v(253.48, -23.1) * mm});
            skLineSegment(sketch, "E196.bottom", {"start": v(220.51, 23.5) * mm, "end": v(221.1, 23.5) * mm});
            skLineSegment(sketch, "E196.top", {"start": v(220.51, -23.5) * mm, "end": v(221.1, -23.5) * mm});
            skLineSegment(sketch, "E196.left", {"start": v(220.51, 23.5) * mm, "end": v(220.51, -23.5) * mm});
            skLineSegment(sketch, "E196.right", {"start": v(221.1, 23.5) * mm, "end": v(221.1, -23.5) * mm});
            skLineSegment(sketch, "E197.bottom", {"start": v(189.93, 23.88) * mm, "end": v(190.51, 23.88) * mm});
            skLineSegment(sketch, "E197.top", {"start": v(189.93, -23.88) * mm, "end": v(190.51, -23.88) * mm});
            skLineSegment(sketch, "E197.left", {"start": v(190.51, 23.88) * mm, "end": v(190.51, -23.88) * mm});
            skLineSegment(sketch, "E197.right", {"start": v(189.93, 23.88) * mm, "end": v(189.93, -23.88) * mm});
            skLineSegment(sketch, "E198.bottom", {"start": v(161.08, 24.24) * mm, "end": v(161.66, 24.24) * mm});
            skLineSegment(sketch, "E198.top", {"start": v(161.08, -24.24) * mm, "end": v(161.66, -24.24) * mm});
            skLineSegment(sketch, "E198.left", {"start": v(161.66, 24.24) * mm, "end": v(161.66, -24.24) * mm});
            skLineSegment(sketch, "E198.right", {"start": v(161.08, 24.24) * mm, "end": v(161.08, -24.24) * mm});
            skLineSegment(sketch, "E199.0.0", {"start": v(-145.9, -28.05) * mm, "end": v(323.85, -22.22) * mm});
            skLineSegment(sketch, "E199.0.1", {"start": v(323.85, -22.22) * mm, "end": v(323.85, 22.23) * mm});
            skLineSegment(sketch, "E199.0.2", {"start": v(323.85, 22.23) * mm, "end": v(-145.9, 28.05) * mm});
            skLineSegment(sketch, "E200.bottom", {"start": v(133.85, 24.58) * mm, "end": v(134.43, 24.58) * mm});
            skLineSegment(sketch, "E200.top", {"start": v(133.85, -24.58) * mm, "end": v(134.43, -24.58) * mm});
            skLineSegment(sketch, "E200.left", {"start": v(134.43, 24.58) * mm, "end": v(134.43, -24.58) * mm});
            skLineSegment(sketch, "E200.right", {"start": v(133.85, 24.58) * mm, "end": v(133.85, -24.58) * mm});
            skLineSegment(sketch, "E201.bottom", {"start": v(108.14, 24.9) * mm, "end": v(108.72, 24.9) * mm});
            skLineSegment(sketch, "E201.top", {"start": v(108.14, -24.9) * mm, "end": v(108.72, -24.9) * mm});
            skLineSegment(sketch, "E201.left", {"start": v(108.72, 24.9) * mm, "end": v(108.72, -24.9) * mm});
            skLineSegment(sketch, "E201.right", {"start": v(108.14, 24.9) * mm, "end": v(108.14, -24.9) * mm});
            skPoint(sketch, "E202.0", {"position": v(0, 26.24) * mm});
            skPoint(sketch, "E203.0", {"position": v(0, -26.24) * mm});
            skPoint(sketch, "E204.0", {"position": v(19.25, 26) * mm});
            skPoint(sketch, "E205.0", {"position": v(39.65, 25.75) * mm});
            skPoint(sketch, "E206.0", {"position": v(61.26, 25.48) * mm});
            skPoint(sketch, "E207.0", {"position": v(84.18, 25.2) * mm});
            skPoint(sketch, "E208.0", {"position": v(84.18, -25.2) * mm});
            skPoint(sketch, "E209.0", {"position": v(61.26, -25.48) * mm});
            skPoint(sketch, "E210.0", {"position": v(39.65, -25.75) * mm});
            skPoint(sketch, "E211.0", {"position": v(19.25, -26) * mm});
            skLineSegment(sketch, "E212.bottom", {"start": v(83.89, 25.2) * mm, "end": v(84.47, 25.2) * mm});
            skLineSegment(sketch, "E212.top", {"start": v(83.89, -25.2) * mm, "end": v(84.47, -25.2) * mm});
            skLineSegment(sketch, "E212.left", {"start": v(84.47, 25.2) * mm, "end": v(84.47, -25.2) * mm});
            skLineSegment(sketch, "E212.right", {"start": v(83.89, 25.2) * mm, "end": v(83.89, -25.2) * mm});
            skLineSegment(sketch, "E213.bottom", {"start": v(60.97, 25.48) * mm, "end": v(61.55, 25.48) * mm});
            skLineSegment(sketch, "E213.top", {"start": v(60.97, -25.48) * mm, "end": v(61.55, -25.48) * mm});
            skLineSegment(sketch, "E213.left", {"start": v(61.55, 25.48) * mm, "end": v(61.55, -25.48) * mm});
            skLineSegment(sketch, "E213.right", {"start": v(60.97, 25.48) * mm, "end": v(60.97, -25.48) * mm});
            skLineSegment(sketch, "E214.bottom", {"start": v(39.36, 25.75) * mm, "end": v(39.94, 25.75) * mm});
            skLineSegment(sketch, "E214.top", {"start": v(39.36, -25.75) * mm, "end": v(39.94, -25.75) * mm});
            skLineSegment(sketch, "E214.left", {"start": v(39.94, 25.75) * mm, "end": v(39.94, -25.75) * mm});
            skLineSegment(sketch, "E214.right", {"start": v(39.36, 25.75) * mm, "end": v(39.36, -25.75) * mm});
            skLineSegment(sketch, "E215.bottom", {"start": v(18.96, 26) * mm, "end": v(19.54, 26) * mm});
            skLineSegment(sketch, "E215.top", {"start": v(18.96, -26) * mm, "end": v(19.54, -26) * mm});
            skLineSegment(sketch, "E215.left", {"start": v(19.54, 26) * mm, "end": v(19.54, -26) * mm});
            skLineSegment(sketch, "E215.right", {"start": v(18.96, 26) * mm, "end": v(18.96, -26) * mm});
            skLineSegment(sketch, "E216.bottom", {"start": v(-0.3, 26.24) * mm, "end": v(0.3, 26.24) * mm});
            skLineSegment(sketch, "E216.top", {"start": v(-0.3, -26.24) * mm, "end": v(0.3, -26.24) * mm});
            skLineSegment(sketch, "E216.left", {"start": v(0.3, 26.24) * mm, "end": v(0.3, -26.24) * mm});
            skLineSegment(sketch, "E216.right", {"start": v(-0.3, 26.24) * mm, "end": v(-0.3, -26.24) * mm});
            skPoint(sketch, "E217.0", {"position": v(-18.19, 26.46) * mm});
            skPoint(sketch, "E218.0", {"position": v(-35.33, 26.68) * mm});
            skPoint(sketch, "E219.0", {"position": v(-51.54, 26.88) * mm});
            skPoint(sketch, "E220.0", {"position": v(-66.83, 27.07) * mm});
            skPoint(sketch, "E221.0", {"position": v(-81.25, 27.24) * mm});
            skPoint(sketch, "E222.0", {"position": v(-94.87, 27.41) * mm});
            skPoint(sketch, "E223.0", {"position": v(-107.72, 27.57) * mm});
            skPoint(sketch, "E224.0", {"position": v(-119.86, 27.72) * mm});
            skPoint(sketch, "E225.0", {"position": v(-131.32, 27.87) * mm});
            skPoint(sketch, "E226.0", {"position": v(-142.11, 28) * mm});
            skPoint(sketch, "E227.0", {"position": v(-142.11, -28) * mm});
            skPoint(sketch, "E228.0", {"position": v(-131.32, -27.87) * mm});
            skPoint(sketch, "E229.0", {"position": v(-120.2, -27.73) * mm});
            skPoint(sketch, "E230.0", {"position": v(-107.72, -27.57) * mm});
            skPoint(sketch, "E231.0", {"position": v(-94.87, -27.41) * mm});
            skPoint(sketch, "E232.0", {"position": v(-81.25, -27.24) * mm});
            skPoint(sketch, "E233.0", {"position": v(-66.83, -27.07) * mm});
            skPoint(sketch, "E234.0", {"position": v(-51.54, -26.88) * mm});
            skPoint(sketch, "E235.0", {"position": v(-35.33, -26.68) * mm});
            skPoint(sketch, "E236.0", {"position": v(-18.19, -26.46) * mm});
            skLineSegment(sketch, "E237.bottom", {"start": v(-18.48, 26.46) * mm, "end": v(-17.9, 26.46) * mm});
            skLineSegment(sketch, "E237.top", {"start": v(-18.48, -26.46) * mm, "end": v(-17.9, -26.46) * mm});
            skLineSegment(sketch, "E237.left", {"start": v(-17.9, 26.46) * mm, "end": v(-17.9, -26.46) * mm});
            skLineSegment(sketch, "E237.right", {"start": v(-18.48, 26.46) * mm, "end": v(-18.48, -26.46) * mm});
            skLineSegment(sketch, "E238.bottom", {"start": v(-35.62, 26.68) * mm, "end": v(-35.04, 26.68) * mm});
            skLineSegment(sketch, "E238.top", {"start": v(-35.62, -26.68) * mm, "end": v(-35.04, -26.68) * mm});
            skLineSegment(sketch, "E238.left", {"start": v(-35.04, 26.68) * mm, "end": v(-35.04, -26.68) * mm});
            skLineSegment(sketch, "E238.right", {"start": v(-35.62, 26.68) * mm, "end": v(-35.62, -26.68) * mm});
            skLineSegment(sketch, "E239.bottom", {"start": v(-51.83, 26.88) * mm, "end": v(-51.25, 26.88) * mm});
            skLineSegment(sketch, "E239.top", {"start": v(-51.83, -26.88) * mm, "end": v(-51.25, -26.88) * mm});
            skLineSegment(sketch, "E239.left", {"start": v(-51.25, 26.88) * mm, "end": v(-51.25, -26.88) * mm});
            skLineSegment(sketch, "E239.right", {"start": v(-51.83, 26.88) * mm, "end": v(-51.83, -26.88) * mm});
            skLineSegment(sketch, "E240.bottom", {"start": v(-67.12, 27.07) * mm, "end": v(-66.54, 27.07) * mm});
            skLineSegment(sketch, "E240.top", {"start": v(-67.12, -27.07) * mm, "end": v(-66.54, -27.07) * mm});
            skLineSegment(sketch, "E240.left", {"start": v(-66.54, 27.07) * mm, "end": v(-66.54, -27.07) * mm});
            skLineSegment(sketch, "E240.right", {"start": v(-67.12, 27.07) * mm, "end": v(-67.12, -27.07) * mm});
            skLineSegment(sketch, "E241.bottom", {"start": v(-81.54, 27.24) * mm, "end": v(-80.96, 27.24) * mm});
            skLineSegment(sketch, "E241.top", {"start": v(-81.54, -27.24) * mm, "end": v(-80.96, -27.24) * mm});
            skLineSegment(sketch, "E241.left", {"start": v(-80.96, 27.24) * mm, "end": v(-80.96, -27.24) * mm});
            skLineSegment(sketch, "E241.right", {"start": v(-81.54, 27.24) * mm, "end": v(-81.54, -27.24) * mm});
            skLineSegment(sketch, "E242.bottom", {"start": v(-95.16, 27.41) * mm, "end": v(-94.58, 27.41) * mm});
            skLineSegment(sketch, "E242.top", {"start": v(-95.16, -27.41) * mm, "end": v(-94.58, -27.41) * mm});
            skLineSegment(sketch, "E242.left", {"start": v(-94.58, 27.41) * mm, "end": v(-94.58, -27.41) * mm});
            skLineSegment(sketch, "E242.right", {"start": v(-95.16, 27.41) * mm, "end": v(-95.16, -27.41) * mm});
            skLineSegment(sketch, "E243.bottom", {"start": v(-108.01, 27.57) * mm, "end": v(-107.43, 27.57) * mm});
            skLineSegment(sketch, "E243.top", {"start": v(-108.01, -27.57) * mm, "end": v(-107.43, -27.57) * mm});
            skLineSegment(sketch, "E243.left", {"start": v(-107.43, 27.57) * mm, "end": v(-107.43, -27.57) * mm});
            skLineSegment(sketch, "E243.right", {"start": v(-108.01, 27.57) * mm, "end": v(-108.01, -27.57) * mm});
            skLineSegment(sketch, "E244.bottom", {"start": v(-131.6, 27.87) * mm, "end": v(-131.03, 27.87) * mm});
            skLineSegment(sketch, "E244.top", {"start": v(-131.6, -27.87) * mm, "end": v(-131.03, -27.87) * mm});
            skLineSegment(sketch, "E244.left", {"start": v(-131.03, 27.87) * mm, "end": v(-131.03, -27.87) * mm});
            skLineSegment(sketch, "E244.right", {"start": v(-131.6, 27.87) * mm, "end": v(-131.6, -27.87) * mm});
            skLineSegment(sketch, "E245.bottom", {"start": v(-142.4, 28) * mm, "end": v(-141.82, 28) * mm});
            skLineSegment(sketch, "E245.top", {"start": v(-142.4, -28) * mm, "end": v(-141.82, -28) * mm});
            skLineSegment(sketch, "E245.left", {"start": v(-141.82, 28) * mm, "end": v(-141.82, -28) * mm});
            skLineSegment(sketch, "E245.right", {"start": v(-142.4, 28) * mm, "end": v(-142.4, -28) * mm});
            skLineSegment(sketch, "E246.bottom", {"start": v(-120.15, 27.73) * mm, "end": v(-119.57, 27.72) * mm});
            skLineSegment(sketch, "E246.top", {"start": v(-120.5, -27.73) * mm, "end": v(-119.92, -27.73) * mm});
            skLineSegment(sketch, "E246.left", {"start": v(-119.57, 27.72) * mm, "end": v(-119.92, -27.73) * mm});
            skLineSegment(sketch, "E246.right", {"start": v(-120.15, 27.73) * mm, "end": v(-120.5, -27.73) * mm});
            skSolve(sketch);
        }
        {
            var Q0;
            {var subQ5=sQuery(id+"F22.wireOp",EDGE,"E181.left");Q0=makeQuery(id+"F22.imprint","IMPRINT",FACE,{"disambiguationData":[TD([[makeQuery(id+"F22.imprint","IMPRINT",EDGE,{"derivedFrom":subQ5}),1.0]])]});}
            var Q1;
            {var subQ7=sQuery(id+"F22.wireOp",EDGE,"E195.left");Q1=makeQuery(id+"F22.imprint","IMPRINT",FACE,{"disambiguationData":[TD([[makeQuery(id+"F22.imprint","IMPRINT",EDGE,{"derivedFrom":subQ7}),1.0]])]});}
            var Q2;
            {var subQ5=sQuery(id+"F22.wireOp",EDGE,"E196.left");Q2=makeQuery(id+"F22.imprint","IMPRINT",FACE,{"disambiguationData":[TD([[makeQuery(id+"F22.imprint","IMPRINT",EDGE,{"derivedFrom":subQ5}),1.0]])]});}
            var Q3;
            {var subQ0=sQuery(id+"F22.wireOp",EDGE,"E197.right");Q3=makeQuery(id+"F22.imprint","IMPRINT",FACE,{"disambiguationData":[TD([[makeQuery(id+"F22.imprint","IMPRINT",EDGE,{"derivedFrom":subQ0}),1.0]])]});}
            var Q4;
            {var subQ0=sQuery(id+"F22.wireOp",EDGE,"E198.right");Q4=makeQuery(id+"F22.imprint","IMPRINT",FACE,{"disambiguationData":[TD([[makeQuery(id+"F22.imprint","IMPRINT",EDGE,{"derivedFrom":subQ0}),1.0]])]});}
            var Q5;
            {var subQ0=sQuery(id+"F22.wireOp",EDGE,"E200.right");Q5=makeQuery(id+"F22.imprint","IMPRINT",FACE,{"disambiguationData":[TD([[makeQuery(id+"F22.imprint","IMPRINT",EDGE,{"derivedFrom":subQ0}),1.0]])]});}
            var Q6;
            {var subQ0=sQuery(id+"F22.wireOp",EDGE,"E201.right");Q6=makeQuery(id+"F22.imprint","IMPRINT",FACE,{"disambiguationData":[TD([[makeQuery(id+"F22.imprint","IMPRINT",EDGE,{"derivedFrom":subQ0}),1.0]])]});}
            var Q7;
            {var subQ0=sQuery(id+"F22.wireOp",EDGE,"E212.right");Q7=makeQuery(id+"F22.imprint","IMPRINT",FACE,{"disambiguationData":[TD([[makeQuery(id+"F22.imprint","IMPRINT",EDGE,{"derivedFrom":subQ0}),1.0]])]});}
            var Q8;
            {var subQ0=sQuery(id+"F22.wireOp",EDGE,"E213.right");Q8=makeQuery(id+"F22.imprint","IMPRINT",FACE,{"disambiguationData":[TD([[makeQuery(id+"F22.imprint","IMPRINT",EDGE,{"derivedFrom":subQ0}),1.0]])]});}
            var Q9;
            {var subQ0=sQuery(id+"F22.wireOp",EDGE,"E214.right");Q9=makeQuery(id+"F22.imprint","IMPRINT",FACE,{"disambiguationData":[TD([[makeQuery(id+"F22.imprint","IMPRINT",EDGE,{"derivedFrom":subQ0}),1.0]])]});}
            var Q10;
            {var subQ0=sQuery(id+"F22.wireOp",EDGE,"E215.right");Q10=makeQuery(id+"F22.imprint","IMPRINT",FACE,{"disambiguationData":[TD([[makeQuery(id+"F22.imprint","IMPRINT",EDGE,{"derivedFrom":subQ0}),1.0]])]});}
            var Q11;
            {var subQ0=sQuery(id+"F22.wireOp",EDGE,"E216.right");Q11=makeQuery(id+"F22.imprint","IMPRINT",FACE,{"disambiguationData":[TD([[makeQuery(id+"F22.imprint","IMPRINT",EDGE,{"derivedFrom":subQ0}),1.0]])]});}
            var Q12;
            {var subQ0=sQuery(id+"F22.wireOp",EDGE,"E237.right");Q12=makeQuery(id+"F22.imprint","IMPRINT",FACE,{"disambiguationData":[TD([[makeQuery(id+"F22.imprint","IMPRINT",EDGE,{"derivedFrom":subQ0}),1.0]])]});}
            var Q13;
            {var subQ0=sQuery(id+"F22.wireOp",EDGE,"E238.right");Q13=makeQuery(id+"F22.imprint","IMPRINT",FACE,{"disambiguationData":[TD([[makeQuery(id+"F22.imprint","IMPRINT",EDGE,{"derivedFrom":subQ0}),1.0]])]});}
            var Q14;
            {var subQ0=sQuery(id+"F22.wireOp",EDGE,"E239.right");Q14=makeQuery(id+"F22.imprint","IMPRINT",FACE,{"disambiguationData":[TD([[makeQuery(id+"F22.imprint","IMPRINT",EDGE,{"derivedFrom":subQ0}),1.0]])]});}
            var Q15;
            {var subQ0=sQuery(id+"F22.wireOp",EDGE,"E240.right");Q15=makeQuery(id+"F22.imprint","IMPRINT",FACE,{"disambiguationData":[TD([[makeQuery(id+"F22.imprint","IMPRINT",EDGE,{"derivedFrom":subQ0}),1.0]])]});}
            var Q16;
            {var subQ0=sQuery(id+"F22.wireOp",EDGE,"E241.right");Q16=makeQuery(id+"F22.imprint","IMPRINT",FACE,{"disambiguationData":[TD([[makeQuery(id+"F22.imprint","IMPRINT",EDGE,{"derivedFrom":subQ0}),1.0]])]});}
            var Q17;
            {var subQ0=sQuery(id+"F22.wireOp",EDGE,"E242.right");Q17=makeQuery(id+"F22.imprint","IMPRINT",FACE,{"disambiguationData":[TD([[makeQuery(id+"F22.imprint","IMPRINT",EDGE,{"derivedFrom":subQ0}),1.0]])]});}
            var Q18;
            {var subQ0=sQuery(id+"F22.wireOp",EDGE,"E243.right");Q18=makeQuery(id+"F22.imprint","IMPRINT",FACE,{"disambiguationData":[TD([[makeQuery(id+"F22.imprint","IMPRINT",EDGE,{"derivedFrom":subQ0}),1.0]])]});}
            var Q19;
            {var subQ0=sQuery(id+"F22.wireOp",EDGE,"E246.right");Q19=makeQuery(id+"F22.imprint","IMPRINT",FACE,{"disambiguationData":[TD([[makeQuery(id+"F22.imprint","IMPRINT",EDGE,{"derivedFrom":subQ0}),1.0]])]});}
            var Q20;
            {var subQ0=sQuery(id+"F22.wireOp",EDGE,"E244.right");Q20=makeQuery(id+"F22.imprint","IMPRINT",FACE,{"disambiguationData":[TD([[makeQuery(id+"F22.imprint","IMPRINT",EDGE,{"derivedFrom":subQ0}),1.0]])]});}
            var Q21;
            {var subQ0=sQuery(id+"F22.wireOp",EDGE,"E245.right");Q21=makeQuery(id+"F22.imprint","IMPRINT",FACE,{"disambiguationData":[TD([[makeQuery(id+"F22.imprint","IMPRINT",EDGE,{"derivedFrom":subQ0}),1.0]])]});}
            extrude(context, id + "F23", {"entities" : qUnion([Q0, Q1, Q2, Q3, Q4, Q5, Q6, Q7, Q8, Q9, Q10, Q11, Q12, Q13, Q14, Q15, Q16, Q17, Q18, Q19, Q20, Q21]), "operationType" : NewBodyOperationType.REMOVE, "oppositeDirection" : true, "depth" : 1.7 * mm});
        }
        {
            var Q0;
            Q0=makeQuery(id+"F21.opExtrude","SWEPT_FACE",FACE,{"disambiguationData":[OSD([sQuery(id+"F20.wireOp",EDGE,"E176")])]});
            var sketch = newSketch(context, id + "F24", { "sketchPlane" : qUnion([Q0])});
            skPoint(sketch, "E247", {"position": v(0, 3) * mm});
            skPoint(sketch, "E248.0", {"position": v(28.05, 3) * mm});
            skPoint(sketch, "E249.0", {"position": v(-28.05, 3) * mm});
            skLineSegment(sketch, "E250", {"start": v(0, 3) * mm, "end": v(0, -301.8) * mm, "construction": true});
            skCircle(sketch, "E251", {"center": v(0, -301.8) * mm, "radius": 304.8 * mm});
            skCircle(sketch, "E252", {"center": v(0, -301.8) * mm, "radius": 306.09 * mm});
            skSolve(sketch);
        }
        {
            var Q0;
            Q0 = qSketchRegion(id + "F24", true);
            extrude(context, id + "F25", {"entities" : qUnion([Q0]), "operationType" : NewBodyOperationType.REMOVE, "oppositeDirection" : true, "depth" : 482.85 * mm});
        }
        {
            var Q0;
            Q0=qCreatedBy(id+"F3.planeOp",FACE);
            var sketch = newSketch(context, id + "F26", { "sketchPlane" : qUnion([Q0])});
            skLineSegment(sketch, "E253", {"start": v(-453.05, 0) * mm, "end": v(-863.38, 0) * mm, "construction": true});
            skPoint(sketch, "E254", {"position": v(-658.21, 0) * mm});
            skPoint(sketch, "E255.0", {"position": v(-453.05, 0) * mm});
            skFitSpline(sketch, "E256", {"points": [v(-453.1, 27.78) * mm, v(-455.78, 31) * mm, v(-458.72, 36.88) * mm, v(-454.44, 47.32) * mm, v(-445.33, 65.26) * mm, v(-440.25, 83.47) * mm, v(-439.71, 104.08) * mm, v(-445.07, 120.42) * mm, v(-454.37, 130.7) * mm, v(-467.9, 137.7) * mm, v(-482.39, 140.9) * mm, v(-496.71, 141.53) * mm, v(-515.34, 139.14) * mm, v(-533.17, 133.73) * mm, v(-551.96, 125.93) * mm, v(-566.28, 119.4) * mm, v(-578.54, 116.37) * mm, v(-594.78, 115.74) * mm, v(-609.27, 117.97) * mm, v(-629.33, 125.45) * mm, v(-639.83, 130.22) * mm, v(-656.49, 138.52) * mm, v(-680.68, 148.7) * mm, v(-700.1, 155.4) * mm, v(-719.37, 160) * mm, v(-734.65, 161.44) * mm, v(-754.87, 162.08) * mm, v(-773.65, 158.26) * mm, v(-789.57, 151.57) * mm, v(-813.15, 135.47) * mm, v(-827, 118.44) * mm, v(-836.7, 97.9) * mm, v(-842.65, 71.87) * mm, v(-845.57, 51.61) * mm, v(-846.7, 18.74) * mm, v(-847.38, -26.51) * mm, v(-846.7, -56.68) * mm, v(-843.77, -86.85) * mm, v(-835.7, -105.44) * mm, v(-824.21, -124.35) * mm, v(-805.08, -144.17) * mm, v(-782.34, -156.1) * mm, v(-745.87, -162.85) * mm, v(-713, -159.02) * mm, v(-681.03, -148.67) * mm, v(-650.18, -135.16) * mm, v(-631.04, -125.7) * mm, v(-613.7, -118.95) * mm, v(-599.3, -115.57) * mm, v(-587.14, -114.45) * mm, v(-571.83, -117.37) * mm, v(-554.72, -124.13) * mm, v(-538.74, -130.88) * mm, v(-526.8, -134.7) * mm, v(-507, -139.25) * mm, v(-489.65, -140.36) * mm, v(-476.11, -139.88) * mm, v(-463.06, -136.7) * mm, v(-452.07, -130.17) * mm, v(-446.18, -121.1) * mm, v(-445.55, -110.75) * mm, v(-449.53, -103.1) * mm, v(-459.56, -96.74) * mm, v(-474.68, -91.49) * mm, v(-488.21, -86.55) * mm, v(-498.72, -80.5) * mm, v(-506.2, -73.97) * mm, v(-512.25, -64.9) * mm, v(-514.38, -50.6) * mm, v(-511.68, -40.91) * mm, v(-502.67, -32.8) * mm, v(-495.24, -28.3) * mm, v(-454.26, 22.58) * mm, v(-453.1, 27.78) * mm]});
            skSolve(sketch);
        }
        {
            var Q0;
            Q0 = qSketchRegion(id + "F26", true);
            extrude(context, id + "F27", {"entities" : qUnion([Q0]), "oppositeDirection" : true, "depth" : 44.45 * mm});
        }
    });
